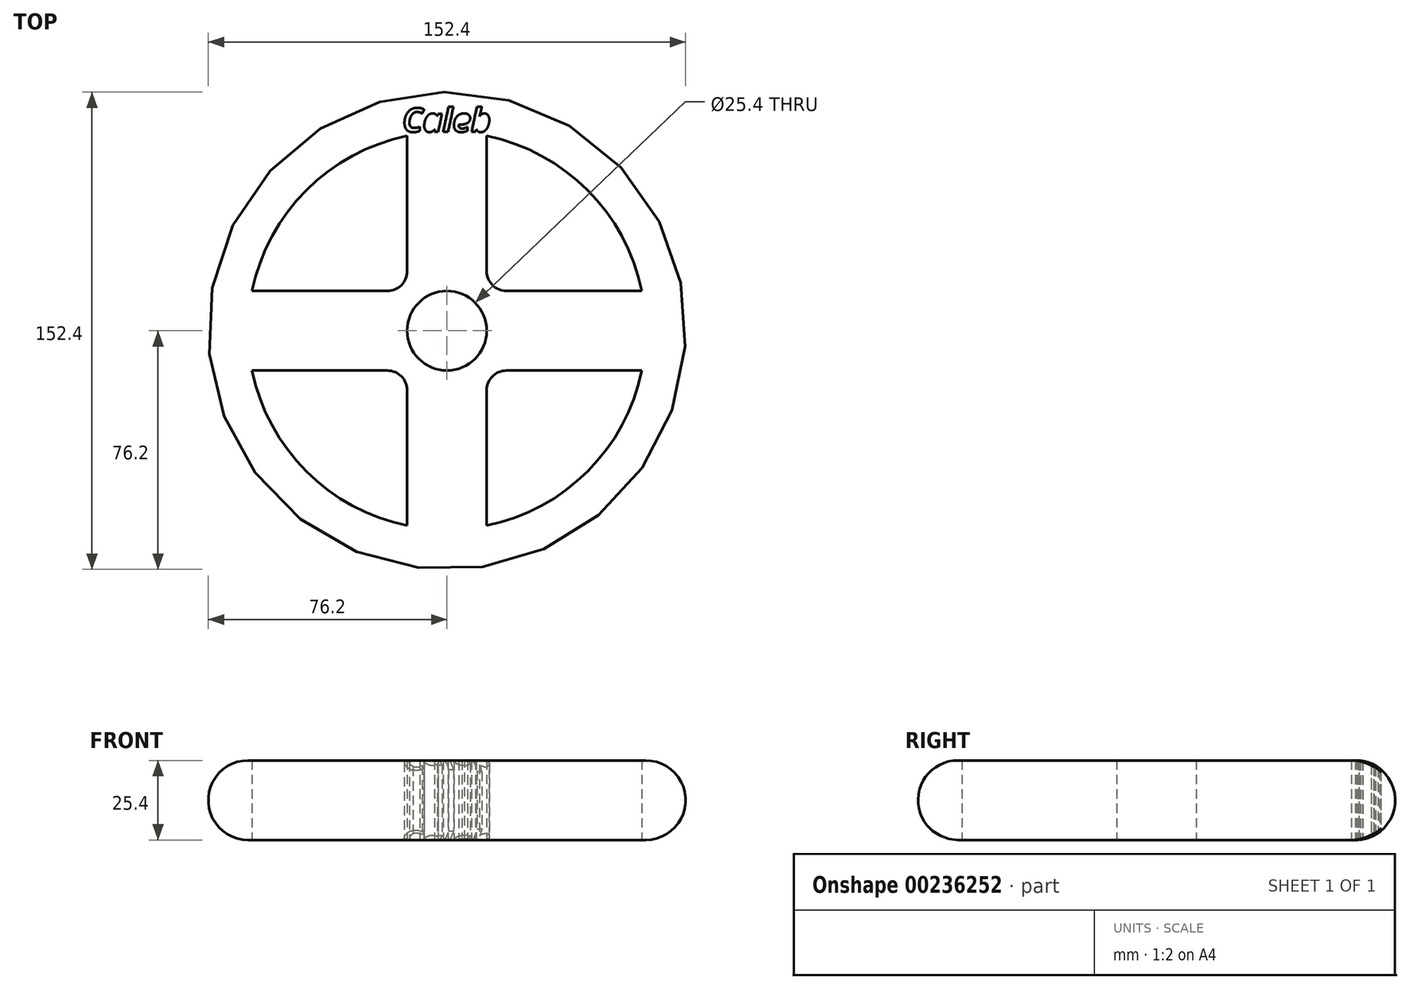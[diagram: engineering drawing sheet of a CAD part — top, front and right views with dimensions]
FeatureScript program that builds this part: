
annotation { "Feature Type Name" : "Feature", "Feature Type Description" : "" }
export const myFeature = defineFeature(function(context is Context, id is Id, definition is map)
    precondition{}
    {
        {
            var Q0;
            Q0=qCreatedBy(makeId("Top.planeOp"),FACE);
            var sketch = newSketch(context, id + "F0", { "sketchPlane" : qUnion([Q0])});
            skCircle(sketch, "E0", {"center": v(0, 0) * mm, "radius": 76.2 * mm});
            skArc(sketch, "E1", {"start": v(62.22, 12.7) * mm, "mid": v(44.9, 44.9) * mm, "end": v(12.7, 62.22) * mm});
            skPoint(sketch, "E2.center.orphan", {"position": v(0, -1.67) * mm});
            skCircle(sketch, "E3", {"center": v(0, 0) * mm, "radius": 12.7 * mm});
            skLineSegment(sketch, "E4", {"start": v(0, 12.7) * mm, "end": v(0, 63.5) * mm});
            skLineSegment(sketch, "E5.0", {"start": v(-12.7, 19.05) * mm, "end": v(-12.7, 62.22) * mm});
            skLineSegment(sketch, "E6.0", {"start": v(12.7, 19.05) * mm, "end": v(12.7, 62.22) * mm});
            skLineSegment(sketch, "E7", {"start": v(0, 0) * mm, "end": v(0, -1.67) * mm});
            skLineSegment(sketch, "E8", {"start": v(-12.7, 0) * mm, "end": v(-63.5, 0) * mm});
            skLineSegment(sketch, "E9", {"start": v(12.7, 0) * mm, "end": v(63.5, 0) * mm});
            skLineSegment(sketch, "E10.0", {"start": v(-19.05, 12.7) * mm, "end": v(-62.22, 12.7) * mm});
            skLineSegment(sketch, "E11.0", {"start": v(-19.05, -12.7) * mm, "end": v(-62.22, -12.7) * mm});
            skLineSegment(sketch, "E12.0", {"start": v(12.7, -19.05) * mm, "end": v(12.7, -62.22) * mm});
            skLineSegment(sketch, "E13.0", {"start": v(-12.7, -19.05) * mm, "end": v(-12.7, -62.22) * mm});
            skLineSegment(sketch, "E14.0", {"start": v(19.05, 12.7) * mm, "end": v(62.22, 12.7) * mm});
            skLineSegment(sketch, "E15.0", {"start": v(19.05, -12.7) * mm, "end": v(62.22, -12.7) * mm});
            skLineSegment(sketch, "E16.trimOffspring", {"start": v(-12.7, -75.13) * mm, "end": v(-12.7, -76.2) * mm});
            skLineSegment(sketch, "E17.trimOffspring", {"start": v(12.7, -75.13) * mm, "end": v(12.7, -76.2) * mm});
            skLineSegment(sketch, "E18.trimOffspring", {"start": v(75.13, -12.7) * mm, "end": v(76.2, -12.7) * mm});
            skLineSegment(sketch, "E19.trimOffspring", {"start": v(75.13, 12.7) * mm, "end": v(76.2, 12.7) * mm});
            skLineSegment(sketch, "E20.trimOffspring", {"start": v(12.7, 75.13) * mm, "end": v(12.7, 76.2) * mm});
            skLineSegment(sketch, "E21.trimOffspring", {"start": v(-12.7, 75.13) * mm, "end": v(-12.7, 76.2) * mm});
            skLineSegment(sketch, "E22.trimOffspring", {"start": v(-75.13, 12.7) * mm, "end": v(-76.2, 12.7) * mm});
            skLineSegment(sketch, "E23.trimOffspring", {"start": v(-75.13, -12.7) * mm, "end": v(-76.2, -12.7) * mm});
            skArc(sketch, "E24.trimOffspring", {"start": v(-62.22, -12.7) * mm, "mid": v(-44.9, -44.9) * mm, "end": v(-12.7, -62.22) * mm});
            skArc(sketch, "E25.trimOffspring", {"start": v(12.7, -62.22) * mm, "mid": v(44.9, -44.9) * mm, "end": v(62.22, -12.7) * mm});
            skArc(sketch, "E26.trimOffspring", {"start": v(-12.7, 62.22) * mm, "mid": v(-44.9, 44.9) * mm, "end": v(-62.22, 12.7) * mm});
            skPoint(sketch, "E27.visualSharp", {"position": v(-12.7, 12.7) * mm});
            skArc(sketch, "E27.filletArc", {"start": v(-19.05, 12.7) * mm, "mid": v(-14.56, 14.56) * mm, "end": v(-12.7, 19.05) * mm});
            skPoint(sketch, "E28.visualSharp", {"position": v(-12.7, -12.7) * mm});
            skArc(sketch, "E28.filletArc", {"start": v(-12.7, -19.05) * mm, "mid": v(-14.56, -14.56) * mm, "end": v(-19.05, -12.7) * mm});
            skPoint(sketch, "E29.visualSharp", {"position": v(12.7, -12.7) * mm});
            skArc(sketch, "E29.filletArc", {"start": v(19.05, -12.7) * mm, "mid": v(14.56, -14.56) * mm, "end": v(12.7, -19.05) * mm});
            skPoint(sketch, "E30.visualSharp", {"position": v(12.7, 12.7) * mm});
            skArc(sketch, "E30.filletArc", {"start": v(12.7, 19.05) * mm, "mid": v(14.56, 14.56) * mm, "end": v(19.05, 12.7) * mm});
            skText(sketch, "E31", { "text": "Caleb\n", "fontName": "OpenSans-BoldItalic.ttf"});
            skLineSegment(sketch, "E32.trimOffspring", {"start": v(0, -12.7) * mm, "end": v(0, -63.5) * mm});
            const initialGuessF0  = {"E31": [-0.01421, 0.0635, 1, 0, 0.00765]};
            skSetInitialGuess(sketch, initialGuessF0);
            skSolve(sketch);
        }
        {
            var Q0;
            Q0 = qSketchRegion(id + "F0", true);
            extrude(context, id + "F1", {"entities" : qUnion([Q0]), "endBound" : BoundingType.SYMMETRIC, "depth" : 25.4 * mm});
        }
        {
            var Q0;
            Q0=makeQuery(id+"F1.opExtrude","SWEPT_FACE",FACE,{"disambiguationData":[OSD([sQuery(id+"F0.wireOp",EDGE,"E0")])]});
            fillet(context, id + "F2", {"entities" : qUnion([Q0]), "radius" : 12.7 * mm, "tangentPropagation" : true, "allowEdgeOverflow" : false});
        }
    });
